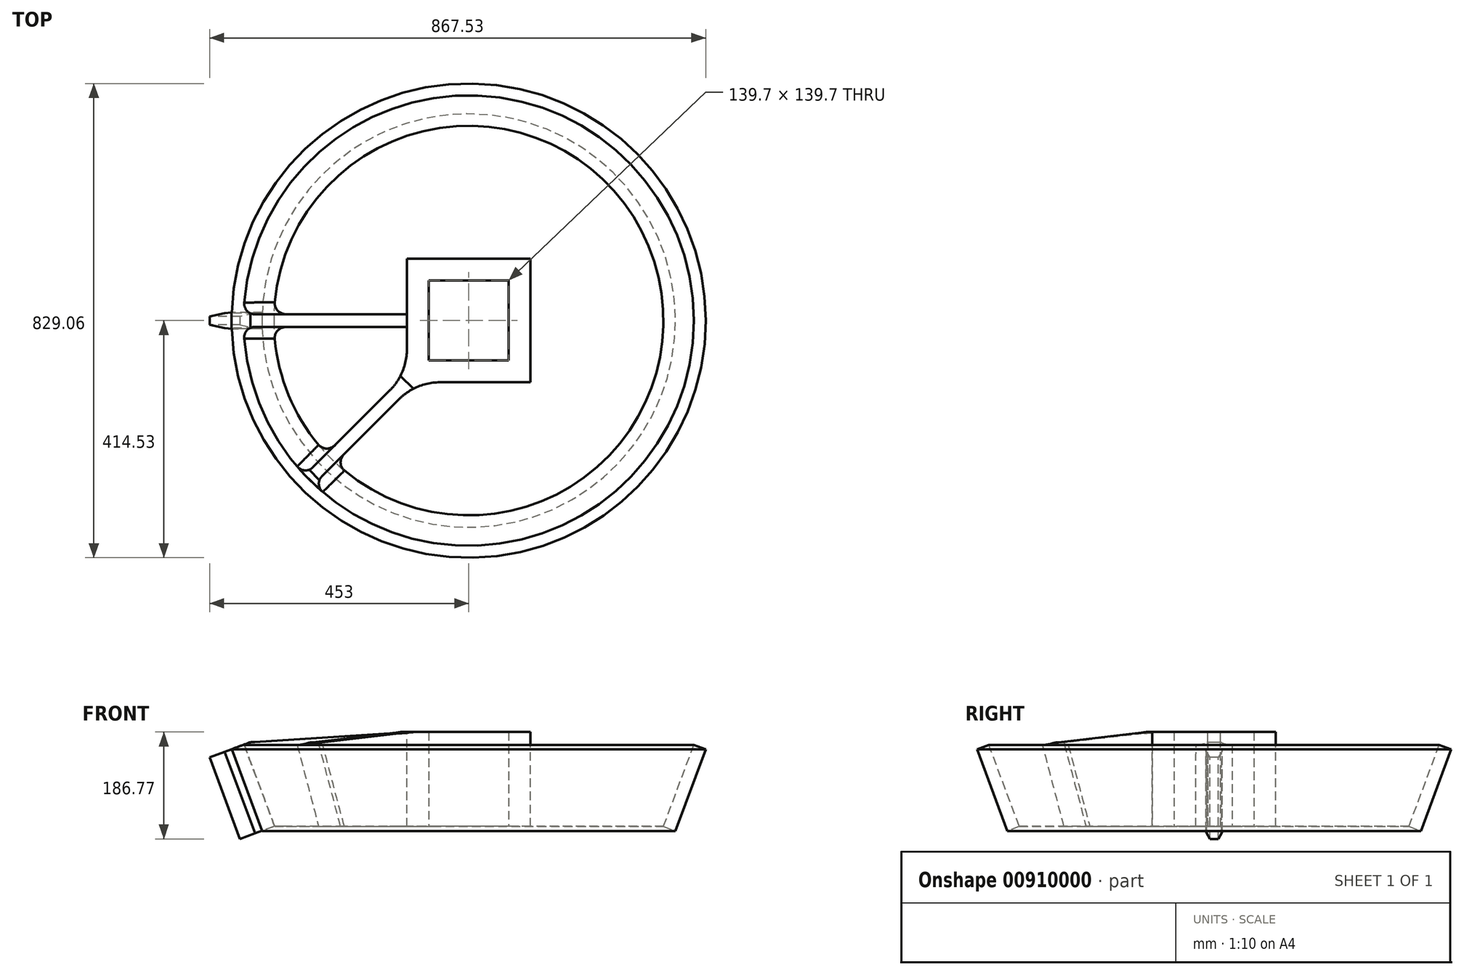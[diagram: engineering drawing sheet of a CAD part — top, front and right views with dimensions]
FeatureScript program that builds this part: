
annotation { "Feature Type Name" : "Feature", "Feature Type Description" : "" }
export const myFeature = defineFeature(function(context is Context, id is Id, definition is map)
    precondition{}
    {
        {
            var Q0;
            Q0=qCreatedBy(makeId("Front.planeOp"),FACE);
            var sketch = newSketch(context, id + "F0", { "sketchPlane" : qUnion([Q0])});
            skLineSegment(sketch, "E0.bottom", {"start": v(107.95, 0) * mm, "end": v(69.85, 0) * mm});
            skLineSegment(sketch, "E0.top", {"start": v(107.95, 165.1) * mm, "end": v(69.85, 165.1) * mm});
            skLineSegment(sketch, "E0.left", {"start": v(107.95, 0) * mm, "end": v(107.95, 165.1) * mm});
            skLineSegment(sketch, "E0.right", {"start": v(-107.95, 0) * mm, "end": v(-107.95, 165.1) * mm});
            skLineSegment(sketch, "E1", {"start": v(-69.85, 165.1) * mm, "end": v(-69.85, 0) * mm});
            skLineSegment(sketch, "E2", {"start": v(69.85, 165.1) * mm, "end": v(69.85, 0) * mm});
            skLineSegment(sketch, "E3", {"start": v(-69.85, 165.1) * mm, "end": v(-107.95, 165.1) * mm});
            skLineSegment(sketch, "E4", {"start": v(69.85, 165.1) * mm, "end": v(-69.85, 165.1) * mm});
            skLineSegment(sketch, "E5", {"start": v(69.85, 0) * mm, "end": v(-69.85, 0) * mm});
            skLineSegment(sketch, "E6", {"start": v(-69.85, 0) * mm, "end": v(-107.95, 0) * mm});
            skLineSegment(sketch, "E7", {"start": v(-340.6, 0) * mm, "end": v(-393.7, 142.85) * mm});
            skLineSegment(sketch, "E8", {"start": v(-393.7, 142.85) * mm, "end": v(-414.53, 135.1) * mm});
            skLineSegment(sketch, "E9", {"start": v(-414.53, 135.1) * mm, "end": v(-361.42, -7.75) * mm});
            skLineSegment(sketch, "E10", {"start": v(-361.42, -7.75) * mm, "end": v(-340.6, 0) * mm});
            skLineSegment(sketch, "E11", {"start": v(0, 0) * mm, "end": v(0, 165.1) * mm, "construction": true});
            skLineSegment(sketch, "E12", {"start": v(-340.6, 0) * mm, "end": v(-107.95, 0) * mm});
            skLineSegment(sketch, "E13", {"start": v(-393.7, 142.85) * mm, "end": v(-381.8, 147.27) * mm});
            skLineSegment(sketch, "E14", {"start": v(-381.8, 147.27) * mm, "end": v(-107.95, 165.1) * mm});
            skLineSegment(sketch, "E15", {"start": v(-381.8, 147.27) * mm, "end": v(-386.22, 159.18) * mm});
            skLineSegment(sketch, "E16", {"start": v(-386.22, 159.18) * mm, "end": v(-418.96, 147) * mm});
            skLineSegment(sketch, "E17", {"start": v(-418.96, 147) * mm, "end": v(-414.53, 135.1) * mm});
            skSolve(sketch);
        }
        {
            var Q0;
            Q0=makeQuery(id+"F0.imprint","IMPRINT",FACE,{"disambiguationData":[TD([[makeQuery(id+"F0.imprint","IMPRINT",EDGE,{"derivedFrom":sQuery(id+"F0.wireOp",EDGE,"E0.right")}),-1.0]])]});
            var Q1;
            Q1=makeQuery(id+"F0.imprint","IMPRINT",FACE,{"disambiguationData":[TD([[makeQuery(id+"F0.imprint","IMPRINT",EDGE,{"derivedFrom":sQuery(id+"F0.wireOp",EDGE,"E1")}),1.0]])]});
            var Q2;
            Q2=makeQuery(id+"F0.imprint","IMPRINT",FACE,{"disambiguationData":[TD([[makeQuery(id+"F0.imprint","IMPRINT",EDGE,{"derivedFrom":sQuery(id+"F0.wireOp",EDGE,"E0.bottom")}),-1.0]])]});
            extrude(context, id + "F1", {"entities" : qUnion([Q0, Q1, Q2]), "depth" : 215.9 * mm, "offsetDistance" : 25 * mm, "symmetric" : true});
        }
        {
            var Q0;
            Q0=makeQuery(id+"F0.imprint","IMPRINT",FACE,{"disambiguationData":[TD([[makeQuery(id+"F0.imprint","IMPRINT",EDGE,{"derivedFrom":sQuery(id+"F0.wireOp",EDGE,"E1")}),1.0]])]});
            extrude(context, id + "F2", {"entities" : qUnion([Q0]), "operationType" : NewBodyOperationType.REMOVE, "oppositeDirection" : true, "depth" : 139.7 * mm, "offsetDistance" : 25 * mm, "symmetric" : true});
        }
        {
            var Q0;
            Q0=makeQuery(id+"F0.imprint","IMPRINT",FACE,{"disambiguationData":[TD([[makeQuery(id+"F0.imprint","IMPRINT",EDGE,{"derivedFrom":sQuery(id+"F0.wireOp",EDGE,"E0.right")}),1.0]])]});
            extrude(context, id + "F3", {"entities" : qUnion([Q0]), "operationType" : NewBodyOperationType.ADD, "depth" : 22.23 * mm, "offsetDistance" : 25 * mm, "symmetric" : true});
        }
        {
            var Q0;
            Q0=makeQuery(id+"F0.imprint","IMPRINT",FACE,{"disambiguationData":[TD([[makeQuery(id+"F0.imprint","IMPRINT",EDGE,{"derivedFrom":sQuery(id+"F0.wireOp",EDGE,"E7")}),1.0]])]});
            var Q1;
            Q1=sQuery(id+"F0.wireOp",EDGE,"E11");
            revolve(context, id + "F4", {"operationType" : NewBodyOperationType.ADD, "surfaceOperationType" : NewSurfaceOperationType.NEW, "entities" : qUnion([Q0]), "axis" : qUnion([Q1]), "revolveType" : RevolveType.FULL});
        }
        {
            var Q0;
            Q0=makeQuery(id+"F1.opExtrude","CAP_VERTEX",VERTEX,{"disambiguationData":[OSD([sQuery(id+"F0.wireOp",EDGE,"E0.right"),sQuery(id+"F0.wireOp",EDGE,"E3"),sQuery(id+"F0.wireOp",EDGE,"E14")])],"isStart":false});
            var Q1;
            Q1=makeQuery(id+"F1.opExtrude","CAP_VERTEX",VERTEX,{"disambiguationData":[OSD([sQuery(id+"F0.wireOp",EDGE,"E0.right"),sQuery(id+"F0.wireOp",EDGE,"E6"),sQuery(id+"F0.wireOp",EDGE,"E12")])],"isStart":false});
            var Q2;
            Q2=makeQuery(id+"F1.opExtrude","CAP_VERTEX",VERTEX,{"disambiguationData":[OSD([sQuery(id+"F0.wireOp",EDGE,"E0.top"),sQuery(id+"F0.wireOp",EDGE,"E0.left")])],"isStart":true});
            cPlane(context, id + "F5", {"entities" : qUnion([Q0, Q1, Q2]), "cplaneType" : CPlaneType.THREE_POINT, "offset" : 25 * mm, "width" : 150 * mm, "height" : 150 * mm});
        }
        {
            var Q0;
            Q0=qCreatedBy(id+"F5.planeOp",FACE);
            var sketch = newSketch(context, id + "F6", { "sketchPlane" : qUnion([Q0])});
            skLineSegment(sketch, "E18", {"start": v(98.78, 165.1) * mm, "end": v(152.66, 165.1) * mm});
            skLineSegment(sketch, "E19", {"start": v(381.8, 146.57) * mm, "end": v(393.7, 142.14) * mm});
            skLineSegment(sketch, "E20", {"start": v(393.7, 142.14) * mm, "end": v(340.85, 0) * mm});
            skLineSegment(sketch, "E21", {"start": v(340.85, 0) * mm, "end": v(98.78, 0) * mm});
            skLineSegment(sketch, "E22", {"start": v(98.78, 0) * mm, "end": v(98.78, 165.1) * mm});
            skLineSegment(sketch, "E23", {"start": v(152.66, 165.1) * mm, "end": v(381.8, 146.57) * mm});
            skSolve(sketch);
        }
        {
            var Q0;
            Q0=makeQuery(id+"F6.imprint","IMPRINT",FACE,{"disambiguationData":[TD([[makeQuery(id+"F6.imprint","IMPRINT",EDGE,{"derivedFrom":sQuery(id+"F6.wireOp",EDGE,"E18")}),-1.0]])]});
            extrude(context, id + "F7", {"entities" : qUnion([Q0]), "operationType" : NewBodyOperationType.ADD, "depth" : 22.23 * mm, "offsetDistance" : 25 * mm, "symmetric" : true});
        }
        {
            var Q0;
            Q0=makeQuery(id+"F3.opExtrude","CAP_EDGE",EDGE,{"disambiguationData":[OSD([sQuery(id+"F0.wireOp",EDGE,"E0.right")])],"isStart":false});
            var Q1;
            Q1=makeQuery(id+"F3.opExtrude","CAP_EDGE",EDGE,{"disambiguationData":[OSD([sQuery(id+"F0.wireOp",EDGE,"E0.right")])],"isStart":true});
            var Q2;
            {var subQ0=sQuery(id+"F0.wireOp",EDGE,"E7");Q2=makeQuery(id+"F4.boolean.opBoolean","INTERSECT",EDGE,{"derivedFrom":[makeQuery(id+"F3.opExtrude","CAP_FACE",FACE,{"disambiguationData":[OSD([sQuery(id+"F0.wireOp",EDGE,"E0.right"),subQ0,sQuery(id+"F0.wireOp",EDGE,"E12"),sQuery(id+"F0.wireOp",EDGE,"E13"),sQuery(id+"F0.wireOp",EDGE,"E14")])],"isStart":true}),makeQuery(id+"F4.opRevolve","SWEPT_FACE",FACE,{"disambiguationData":[OSD([subQ0])]})]});}
            var Q3;
            {var subQ0=sQuery(id+"F0.wireOp",EDGE,"E7");Q3=makeQuery(id+"F4.boolean.opBoolean","INTERSECT",EDGE,{"derivedFrom":[makeQuery(id+"F3.opExtrude","CAP_FACE",FACE,{"disambiguationData":[OSD([sQuery(id+"F0.wireOp",EDGE,"E0.right"),subQ0,sQuery(id+"F0.wireOp",EDGE,"E12"),sQuery(id+"F0.wireOp",EDGE,"E13"),sQuery(id+"F0.wireOp",EDGE,"E14")])],"isStart":false}),makeQuery(id+"F4.opRevolve","SWEPT_FACE",FACE,{"disambiguationData":[OSD([subQ0])]})]});}
            var Q4;
            Q4=makeQuery(id+"F7.boolean.opBoolean","INTERSECT",EDGE,{"derivedFrom":[makeQuery(id+"F4.opRevolve","SWEPT_FACE",FACE,{"disambiguationData":[OSD([sQuery(id+"F0.wireOp",EDGE,"E7")])]}),makeQuery(id+"F7.opExtrude","CAP_FACE",FACE,{"disambiguationData":[OSD([sQuery(id+"F6.wireOp",EDGE,"E18"),sQuery(id+"F6.wireOp",EDGE,"E19"),sQuery(id+"F6.wireOp",EDGE,"E20"),sQuery(id+"F6.wireOp",EDGE,"E21"),sQuery(id+"F6.wireOp",EDGE,"E22"),sQuery(id+"F6.wireOp",EDGE,"E23")])],"isStart":false})]});
            var Q5;
            Q5=makeQuery(id+"F7.boolean.opBoolean","INTERSECT",EDGE,{"derivedFrom":[makeQuery(id+"F4.opRevolve","SWEPT_FACE",FACE,{"disambiguationData":[OSD([sQuery(id+"F0.wireOp",EDGE,"E7")])]}),makeQuery(id+"F7.opExtrude","CAP_FACE",FACE,{"disambiguationData":[OSD([sQuery(id+"F6.wireOp",EDGE,"E18"),sQuery(id+"F6.wireOp",EDGE,"E19"),sQuery(id+"F6.wireOp",EDGE,"E20"),sQuery(id+"F6.wireOp",EDGE,"E21"),sQuery(id+"F6.wireOp",EDGE,"E22"),sQuery(id+"F6.wireOp",EDGE,"E23")])],"isStart":true})]});
            var Q6;
            {var subQ0=sQuery(id+"F6.wireOp",EDGE,"E21");var subQ2=sQuery(id+"F0.wireOp",EDGE,"E12");var subQ9=sQuery(id+"F0.wireOp",EDGE,"E14");var subQ10=sQuery(id+"F0.wireOp",EDGE,"E13");var subQ11=sQuery(id+"F0.wireOp",EDGE,"E7");var subQ12=sQuery(id+"F0.wireOp",EDGE,"E0.right");var subQ13=makeQuery(id+"F3.opExtrude","CAP_FACE",FACE,{"disambiguationData":[OSD([subQ12,subQ11,subQ2,subQ10,subQ9])],"isStart":true});Q6=makeQuery(id+"FeQxwqO8TE0xPhn_1.3.F7.boolean.opBoolean","INTERSECT",EDGE,{"derivedFrom":[makeQuery(id+"FeQxwqO8TE0xPhn_1.3.F3.boolean.opBoolean","SPLIT",FACE,{"disambiguationData":[TD([subQ13])],"derivedFrom":makeQuery(id+"FeQxwqO8TE0xPhn_1.2.F3.boolean.opBoolean","SPLIT",FACE,{"disambiguationData":[TD([subQ13])],"derivedFrom":makeQuery(id+"FeQxwqO8TE0xPhn_1.1.F3.boolean.opBoolean","SPLIT",FACE,{"disambiguationData":[TD([subQ13])],"derivedFrom":makeQuery(id+"F4.opRevolve","SWEPT_FACE",FACE,{"disambiguationData":[OSD([subQ11])]})})})}),makeQuery(id+"FeQxwqO8TE0xPhn_1.3.F7.opExtrude","CAP_FACE",FACE,{"disambiguationData":[OSD([sQuery(id+"F6.wireOp",EDGE,"E18"),sQuery(id+"F6.wireOp",EDGE,"E19"),sQuery(id+"F6.wireOp",EDGE,"E20"),subQ0,sQuery(id+"F6.wireOp",EDGE,"E22"),sQuery(id+"F6.wireOp",EDGE,"E23")])],"isStart":true})]});}
            var Q7;
            {var subQ0=sQuery(id+"F6.wireOp",EDGE,"E21");var subQ2=sQuery(id+"F0.wireOp",EDGE,"E12");var subQ9=sQuery(id+"F0.wireOp",EDGE,"E14");var subQ10=sQuery(id+"F0.wireOp",EDGE,"E13");var subQ11=sQuery(id+"F0.wireOp",EDGE,"E7");var subQ12=sQuery(id+"F0.wireOp",EDGE,"E0.right");var subQ13=makeQuery(id+"F3.opExtrude","CAP_FACE",FACE,{"disambiguationData":[OSD([subQ12,subQ11,subQ2,subQ10,subQ9])],"isStart":true});Q7=makeQuery(id+"FeQxwqO8TE0xPhn_1.3.F7.boolean.opBoolean","INTERSECT",EDGE,{"derivedFrom":[makeQuery(id+"FeQxwqO8TE0xPhn_1.3.F3.boolean.opBoolean","SPLIT",FACE,{"disambiguationData":[TD([subQ13])],"derivedFrom":makeQuery(id+"FeQxwqO8TE0xPhn_1.2.F3.boolean.opBoolean","SPLIT",FACE,{"disambiguationData":[TD([subQ13])],"derivedFrom":makeQuery(id+"FeQxwqO8TE0xPhn_1.1.F3.boolean.opBoolean","SPLIT",FACE,{"disambiguationData":[TD([subQ13])],"derivedFrom":makeQuery(id+"F4.opRevolve","SWEPT_FACE",FACE,{"disambiguationData":[OSD([subQ11])]})})})}),makeQuery(id+"FeQxwqO8TE0xPhn_1.3.F7.opExtrude","CAP_FACE",FACE,{"disambiguationData":[OSD([sQuery(id+"F6.wireOp",EDGE,"E18"),sQuery(id+"F6.wireOp",EDGE,"E19"),sQuery(id+"F6.wireOp",EDGE,"E20"),subQ0,sQuery(id+"F6.wireOp",EDGE,"E22"),sQuery(id+"F6.wireOp",EDGE,"E23")])],"isStart":false})]});}
            var Q8;
            {var subQ0=sQuery(id+"F0.wireOp",EDGE,"E14");var subQ1=sQuery(id+"F0.wireOp",EDGE,"E13");var subQ2=sQuery(id+"F0.wireOp",EDGE,"E12");var subQ3=sQuery(id+"F0.wireOp",EDGE,"E7");var subQ4=sQuery(id+"F0.wireOp",EDGE,"E0.right");var subQ6=makeQuery(id+"F3.opExtrude","CAP_FACE",FACE,{"disambiguationData":[OSD([subQ4,subQ3,subQ2,subQ1,subQ0])],"isStart":true});Q8=makeQuery(id+"FeQxwqO8TE0xPhn_1.3.F3.boolean.opBoolean","INTERSECT",EDGE,{"derivedFrom":[makeQuery(id+"FeQxwqO8TE0xPhn_1.2.F3.boolean.opBoolean","SPLIT",FACE,{"disambiguationData":[TD([subQ6])],"derivedFrom":makeQuery(id+"FeQxwqO8TE0xPhn_1.1.F3.boolean.opBoolean","SPLIT",FACE,{"disambiguationData":[TD([subQ6])],"derivedFrom":makeQuery(id+"F4.opRevolve","SWEPT_FACE",FACE,{"disambiguationData":[OSD([subQ3])]})})}),makeQuery(id+"FeQxwqO8TE0xPhn_1.3.F3.opExtrude","CAP_FACE",FACE,{"disambiguationData":[OSD([subQ4,subQ3,subQ2,subQ1,subQ0])],"isStart":false})]});}
            var Q9;
            {var subQ0=sQuery(id+"F0.wireOp",EDGE,"E14");var subQ1=sQuery(id+"F0.wireOp",EDGE,"E13");var subQ2=sQuery(id+"F0.wireOp",EDGE,"E12");var subQ3=sQuery(id+"F0.wireOp",EDGE,"E7");var subQ4=sQuery(id+"F0.wireOp",EDGE,"E0.right");var subQ6=makeQuery(id+"F3.opExtrude","CAP_FACE",FACE,{"disambiguationData":[OSD([subQ4,subQ3,subQ2,subQ1,subQ0])],"isStart":true});Q9=makeQuery(id+"FeQxwqO8TE0xPhn_1.3.F3.boolean.opBoolean","INTERSECT",EDGE,{"derivedFrom":[makeQuery(id+"FeQxwqO8TE0xPhn_1.2.F3.boolean.opBoolean","SPLIT",FACE,{"disambiguationData":[TD([subQ6])],"derivedFrom":makeQuery(id+"FeQxwqO8TE0xPhn_1.1.F3.boolean.opBoolean","SPLIT",FACE,{"disambiguationData":[TD([subQ6])],"derivedFrom":makeQuery(id+"F4.opRevolve","SWEPT_FACE",FACE,{"disambiguationData":[OSD([subQ3])]})})}),makeQuery(id+"FeQxwqO8TE0xPhn_1.3.F3.opExtrude","CAP_FACE",FACE,{"disambiguationData":[OSD([subQ4,subQ3,subQ2,subQ1,subQ0])],"isStart":true})]});}
            var Q10;
            Q10=makeQuery(id+"FeQxwqO8TE0xPhn_1.3.F3.opExtrude","CAP_EDGE",EDGE,{"disambiguationData":[OSD([sQuery(id+"F0.wireOp",EDGE,"E0.right")])],"isStart":true});
            var Q11;
            Q11=makeQuery(id+"FeQxwqO8TE0xPhn_1.3.F3.opExtrude","CAP_EDGE",EDGE,{"disambiguationData":[OSD([sQuery(id+"F0.wireOp",EDGE,"E0.right")])],"isStart":false});
            var Q12;
            {var subQ0=sQuery(id+"F6.wireOp",EDGE,"E21");var subQ2=sQuery(id+"F0.wireOp",EDGE,"E14");var subQ3=sQuery(id+"F0.wireOp",EDGE,"E13");var subQ4=sQuery(id+"F0.wireOp",EDGE,"E12");var subQ5=sQuery(id+"F0.wireOp",EDGE,"E7");var subQ6=sQuery(id+"F0.wireOp",EDGE,"E0.right");var subQ7=makeQuery(id+"F3.opExtrude","CAP_FACE",FACE,{"disambiguationData":[OSD([subQ6,subQ5,subQ4,subQ3,subQ2])],"isStart":true});Q12=makeQuery(id+"FeQxwqO8TE0xPhn_1.2.F7.boolean.opBoolean","INTERSECT",EDGE,{"derivedFrom":[makeQuery(id+"FeQxwqO8TE0xPhn_1.2.F3.boolean.opBoolean","SPLIT",FACE,{"disambiguationData":[TD([subQ7])],"derivedFrom":makeQuery(id+"FeQxwqO8TE0xPhn_1.1.F3.boolean.opBoolean","SPLIT",FACE,{"disambiguationData":[TD([subQ7])],"derivedFrom":makeQuery(id+"F4.opRevolve","SWEPT_FACE",FACE,{"disambiguationData":[OSD([subQ5])]})})}),makeQuery(id+"FeQxwqO8TE0xPhn_1.2.F7.opExtrude","CAP_FACE",FACE,{"disambiguationData":[OSD([sQuery(id+"F6.wireOp",EDGE,"E18"),sQuery(id+"F6.wireOp",EDGE,"E19"),sQuery(id+"F6.wireOp",EDGE,"E20"),subQ0,sQuery(id+"F6.wireOp",EDGE,"E22"),sQuery(id+"F6.wireOp",EDGE,"E23")])],"isStart":true})]});}
            var Q13;
            {var subQ0=sQuery(id+"F6.wireOp",EDGE,"E21");var subQ2=sQuery(id+"F0.wireOp",EDGE,"E14");var subQ3=sQuery(id+"F0.wireOp",EDGE,"E13");var subQ4=sQuery(id+"F0.wireOp",EDGE,"E12");var subQ5=sQuery(id+"F0.wireOp",EDGE,"E7");var subQ6=sQuery(id+"F0.wireOp",EDGE,"E0.right");var subQ7=makeQuery(id+"F3.opExtrude","CAP_FACE",FACE,{"disambiguationData":[OSD([subQ6,subQ5,subQ4,subQ3,subQ2])],"isStart":true});Q13=makeQuery(id+"FeQxwqO8TE0xPhn_1.2.F7.boolean.opBoolean","INTERSECT",EDGE,{"derivedFrom":[makeQuery(id+"FeQxwqO8TE0xPhn_1.2.F3.boolean.opBoolean","SPLIT",FACE,{"disambiguationData":[TD([subQ7])],"derivedFrom":makeQuery(id+"FeQxwqO8TE0xPhn_1.1.F3.boolean.opBoolean","SPLIT",FACE,{"disambiguationData":[TD([subQ7])],"derivedFrom":makeQuery(id+"F4.opRevolve","SWEPT_FACE",FACE,{"disambiguationData":[OSD([subQ5])]})})}),makeQuery(id+"FeQxwqO8TE0xPhn_1.2.F7.opExtrude","CAP_FACE",FACE,{"disambiguationData":[OSD([sQuery(id+"F6.wireOp",EDGE,"E18"),sQuery(id+"F6.wireOp",EDGE,"E19"),sQuery(id+"F6.wireOp",EDGE,"E20"),subQ0,sQuery(id+"F6.wireOp",EDGE,"E22"),sQuery(id+"F6.wireOp",EDGE,"E23")])],"isStart":false})]});}
            var Q14;
            Q14=makeQuery(id+"FeQxwqO8TE0xPhn_1.2.F3.opExtrude","CAP_EDGE",EDGE,{"disambiguationData":[OSD([sQuery(id+"F0.wireOp",EDGE,"E0.right")])],"isStart":false});
            var Q15;
            {var subQ0=sQuery(id+"F0.wireOp",EDGE,"E14");var subQ1=sQuery(id+"F0.wireOp",EDGE,"E13");var subQ2=sQuery(id+"F0.wireOp",EDGE,"E12");var subQ3=sQuery(id+"F0.wireOp",EDGE,"E7");var subQ4=sQuery(id+"F0.wireOp",EDGE,"E0.right");Q15=makeQuery(id+"FeQxwqO8TE0xPhn_1.2.F3.boolean.opBoolean","INTERSECT",EDGE,{"derivedFrom":[makeQuery(id+"FeQxwqO8TE0xPhn_1.1.F3.boolean.opBoolean","SPLIT",FACE,{"disambiguationData":[TD([makeQuery(id+"F3.opExtrude","CAP_FACE",FACE,{"disambiguationData":[OSD([subQ4,subQ3,subQ2,subQ1,subQ0])],"isStart":true})])],"derivedFrom":makeQuery(id+"F4.opRevolve","SWEPT_FACE",FACE,{"disambiguationData":[OSD([subQ3])]})}),makeQuery(id+"FeQxwqO8TE0xPhn_1.2.F3.opExtrude","CAP_FACE",FACE,{"disambiguationData":[OSD([subQ4,subQ3,subQ2,subQ1,subQ0])],"isStart":false})]});}
            var Q16;
            Q16=makeQuery(id+"FeQxwqO8TE0xPhn_1.2.F3.opExtrude","CAP_EDGE",EDGE,{"disambiguationData":[OSD([sQuery(id+"F0.wireOp",EDGE,"E0.right")])],"isStart":true});
            var Q17;
            Q17=makeQuery(id+"FeQxwqO8TE0xPhn_1.1.F3.opExtrude","CAP_EDGE",EDGE,{"disambiguationData":[OSD([sQuery(id+"F0.wireOp",EDGE,"E0.right")])],"isStart":false});
            var Q18;
            Q18=makeQuery(id+"FeQxwqO8TE0xPhn_1.1.F3.opExtrude","CAP_EDGE",EDGE,{"disambiguationData":[OSD([sQuery(id+"F0.wireOp",EDGE,"E0.right")])],"isStart":true});
            var Q19;
            {var subQ0=sQuery(id+"F0.wireOp",EDGE,"E7");Q19=makeQuery(id+"FeQxwqO8TE0xPhn_1.1.F3.boolean.opBoolean","INTERSECT",EDGE,{"derivedFrom":[makeQuery(id+"F4.opRevolve","SWEPT_FACE",FACE,{"disambiguationData":[OSD([subQ0])]}),makeQuery(id+"FeQxwqO8TE0xPhn_1.1.F3.opExtrude","CAP_FACE",FACE,{"disambiguationData":[OSD([sQuery(id+"F0.wireOp",EDGE,"E0.right"),subQ0,sQuery(id+"F0.wireOp",EDGE,"E12"),sQuery(id+"F0.wireOp",EDGE,"E13"),sQuery(id+"F0.wireOp",EDGE,"E14")])],"isStart":true})]});}
            var Q20;
            {var subQ0=sQuery(id+"F6.wireOp",EDGE,"E21");var subQ1=sQuery(id+"F0.wireOp",EDGE,"E14");var subQ2=sQuery(id+"F0.wireOp",EDGE,"E13");var subQ3=sQuery(id+"F0.wireOp",EDGE,"E12");var subQ4=sQuery(id+"F0.wireOp",EDGE,"E7");var subQ5=sQuery(id+"F0.wireOp",EDGE,"E0.right");Q20=makeQuery(id+"FeQxwqO8TE0xPhn_1.1.F7.boolean.opBoolean","INTERSECT",EDGE,{"derivedFrom":[makeQuery(id+"FeQxwqO8TE0xPhn_1.1.F3.boolean.opBoolean","SPLIT",FACE,{"disambiguationData":[TD([makeQuery(id+"F3.opExtrude","CAP_FACE",FACE,{"disambiguationData":[OSD([subQ5,subQ4,subQ3,subQ2,subQ1])],"isStart":true})])],"derivedFrom":makeQuery(id+"F4.opRevolve","SWEPT_FACE",FACE,{"disambiguationData":[OSD([subQ4])]})}),makeQuery(id+"FeQxwqO8TE0xPhn_1.1.F7.opExtrude","CAP_FACE",FACE,{"disambiguationData":[OSD([sQuery(id+"F6.wireOp",EDGE,"E18"),sQuery(id+"F6.wireOp",EDGE,"E19"),sQuery(id+"F6.wireOp",EDGE,"E20"),subQ0,sQuery(id+"F6.wireOp",EDGE,"E22"),sQuery(id+"F6.wireOp",EDGE,"E23")])],"isStart":false})]});}
            var Q21;
            {var subQ0=sQuery(id+"F0.wireOp",EDGE,"E14");var subQ1=sQuery(id+"F0.wireOp",EDGE,"E13");var subQ2=sQuery(id+"F0.wireOp",EDGE,"E12");var subQ3=sQuery(id+"F0.wireOp",EDGE,"E7");var subQ4=sQuery(id+"F0.wireOp",EDGE,"E0.right");Q21=makeQuery(id+"FeQxwqO8TE0xPhn_1.2.F3.boolean.opBoolean","INTERSECT",EDGE,{"derivedFrom":[makeQuery(id+"FeQxwqO8TE0xPhn_1.1.F3.boolean.opBoolean","SPLIT",FACE,{"disambiguationData":[TD([makeQuery(id+"F3.opExtrude","CAP_FACE",FACE,{"disambiguationData":[OSD([subQ4,subQ3,subQ2,subQ1,subQ0])],"isStart":true})])],"derivedFrom":makeQuery(id+"F4.opRevolve","SWEPT_FACE",FACE,{"disambiguationData":[OSD([subQ3])]})}),makeQuery(id+"FeQxwqO8TE0xPhn_1.2.F3.opExtrude","CAP_FACE",FACE,{"disambiguationData":[OSD([subQ4,subQ3,subQ2,subQ1,subQ0])],"isStart":true})]});}
            var Q22;
            {var subQ0=sQuery(id+"F6.wireOp",EDGE,"E21");var subQ1=sQuery(id+"F0.wireOp",EDGE,"E14");var subQ2=sQuery(id+"F0.wireOp",EDGE,"E13");var subQ3=sQuery(id+"F0.wireOp",EDGE,"E12");var subQ4=sQuery(id+"F0.wireOp",EDGE,"E7");var subQ5=sQuery(id+"F0.wireOp",EDGE,"E0.right");Q22=makeQuery(id+"FeQxwqO8TE0xPhn_1.1.F7.boolean.opBoolean","INTERSECT",EDGE,{"derivedFrom":[makeQuery(id+"FeQxwqO8TE0xPhn_1.1.F3.boolean.opBoolean","SPLIT",FACE,{"disambiguationData":[TD([makeQuery(id+"F3.opExtrude","CAP_FACE",FACE,{"disambiguationData":[OSD([subQ5,subQ4,subQ3,subQ2,subQ1])],"isStart":true})])],"derivedFrom":makeQuery(id+"F4.opRevolve","SWEPT_FACE",FACE,{"disambiguationData":[OSD([subQ4])]})}),makeQuery(id+"FeQxwqO8TE0xPhn_1.1.F7.opExtrude","CAP_FACE",FACE,{"disambiguationData":[OSD([sQuery(id+"F6.wireOp",EDGE,"E18"),sQuery(id+"F6.wireOp",EDGE,"E19"),sQuery(id+"F6.wireOp",EDGE,"E20"),subQ0,sQuery(id+"F6.wireOp",EDGE,"E22"),sQuery(id+"F6.wireOp",EDGE,"E23")])],"isStart":true})]});}
            var Q23;
            {var subQ0=sQuery(id+"F0.wireOp",EDGE,"E7");Q23=makeQuery(id+"FeQxwqO8TE0xPhn_1.1.F3.boolean.opBoolean","INTERSECT",EDGE,{"derivedFrom":[makeQuery(id+"F4.opRevolve","SWEPT_FACE",FACE,{"disambiguationData":[OSD([subQ0])]}),makeQuery(id+"FeQxwqO8TE0xPhn_1.1.F3.opExtrude","CAP_FACE",FACE,{"disambiguationData":[OSD([sQuery(id+"F0.wireOp",EDGE,"E0.right"),subQ0,sQuery(id+"F0.wireOp",EDGE,"E12"),sQuery(id+"F0.wireOp",EDGE,"E13"),sQuery(id+"F0.wireOp",EDGE,"E14")])],"isStart":false})]});}
            fillet(context, id + "F8", {"entities" : qUnion([Q0, Q1, Q2, Q3, Q4, Q5, Q6, Q7, Q8, Q9, Q10, Q11, Q12, Q13, Q14, Q15, Q16, Q17, Q18, Q19, Q20, Q21, Q22, Q23]), "radius" : 19.05 * mm, "tangentPropagation" : true, "allowEdgeOverflow" : false});
        }
        {
            var Q0;
            Q0=makeQuery(id+"F7.boolean.opBoolean","INTERSECT",EDGE,{"derivedFrom":[makeQuery(id+"F1.opExtrude","CAP_FACE",FACE,{"disambiguationData":[OSD([sQuery(id+"F0.wireOp",EDGE,"E0.bottom"),sQuery(id+"F0.wireOp",EDGE,"E0.top"),sQuery(id+"F0.wireOp",EDGE,"E0.left"),sQuery(id+"F0.wireOp",EDGE,"E0.right"),sQuery(id+"F0.wireOp",EDGE,"E3"),sQuery(id+"F0.wireOp",EDGE,"E4"),sQuery(id+"F0.wireOp",EDGE,"E5"),sQuery(id+"F0.wireOp",EDGE,"E6")])],"isStart":false}),makeQuery(id+"F7.opExtrude","CAP_FACE",FACE,{"disambiguationData":[OSD([sQuery(id+"F6.wireOp",EDGE,"E18"),sQuery(id+"F6.wireOp",EDGE,"E19"),sQuery(id+"F6.wireOp",EDGE,"E20"),sQuery(id+"F6.wireOp",EDGE,"E21"),sQuery(id+"F6.wireOp",EDGE,"E22"),sQuery(id+"F6.wireOp",EDGE,"E23")])],"isStart":true})]});
            var Q1;
            {var subQ0=sQuery(id+"F0.wireOp",EDGE,"E14");var subQ1=sQuery(id+"F0.wireOp",EDGE,"E12");var subQ2=sQuery(id+"F0.wireOp",EDGE,"E0.right");Q1=makeQuery(id+"F7.boolean.opBoolean","INTERSECT",EDGE,{"derivedFrom":[makeQuery(id+"F3.boolean.opBoolean","SPLIT",FACE,{"disambiguationData":[TD([makeQuery(id+"F3.opExtrude","CAP_FACE",FACE,{"disambiguationData":[OSD([subQ2,sQuery(id+"F0.wireOp",EDGE,"E7"),subQ1,sQuery(id+"F0.wireOp",EDGE,"E13"),subQ0])],"isStart":false})])],"derivedFrom":makeQuery(id+"F1.opExtrude","SWEPT_FACE",FACE,{"disambiguationData":[OSD([subQ2])]})}),makeQuery(id+"F7.opExtrude","CAP_FACE",FACE,{"disambiguationData":[OSD([sQuery(id+"F6.wireOp",EDGE,"E18"),sQuery(id+"F6.wireOp",EDGE,"E19"),sQuery(id+"F6.wireOp",EDGE,"E20"),sQuery(id+"F6.wireOp",EDGE,"E21"),sQuery(id+"F6.wireOp",EDGE,"E22"),sQuery(id+"F6.wireOp",EDGE,"E23")])],"isStart":false})]});}
            var Q2;
            {var subQ0=sQuery(id+"F0.wireOp",EDGE,"E14");var subQ1=sQuery(id+"F0.wireOp",EDGE,"E12");var subQ2=sQuery(id+"F0.wireOp",EDGE,"E0.right");Q2=makeQuery(id+"FeQxwqO8TE0xPhn_1.3.F7.boolean.opBoolean","INTERSECT",EDGE,{"derivedFrom":[makeQuery(id+"F3.boolean.opBoolean","SPLIT",FACE,{"disambiguationData":[TD([makeQuery(id+"F3.opExtrude","CAP_FACE",FACE,{"disambiguationData":[OSD([subQ2,sQuery(id+"F0.wireOp",EDGE,"E7"),subQ1,sQuery(id+"F0.wireOp",EDGE,"E13"),subQ0])],"isStart":true})])],"derivedFrom":makeQuery(id+"F1.opExtrude","SWEPT_FACE",FACE,{"disambiguationData":[OSD([subQ2])]})}),makeQuery(id+"FeQxwqO8TE0xPhn_1.3.F7.opExtrude","CAP_FACE",FACE,{"disambiguationData":[OSD([sQuery(id+"F6.wireOp",EDGE,"E18"),sQuery(id+"F6.wireOp",EDGE,"E19"),sQuery(id+"F6.wireOp",EDGE,"E20"),sQuery(id+"F6.wireOp",EDGE,"E21"),sQuery(id+"F6.wireOp",EDGE,"E22"),sQuery(id+"F6.wireOp",EDGE,"E23")])],"isStart":true})]});}
            var Q3;
            {var subQ0=sQuery(id+"F6.wireOp",EDGE,"E21");var subQ1=sQuery(id+"F6.wireOp",EDGE,"E18");var subQ3=sQuery(id+"F0.wireOp",EDGE,"E4");var subQ4=sQuery(id+"F0.wireOp",EDGE,"E3");var subQ5=sQuery(id+"F0.wireOp",EDGE,"E0.top");var subQ7=sQuery(id+"F0.wireOp",EDGE,"E0.right");var subQ8=sQuery(id+"F0.wireOp",EDGE,"E6");var subQ9=sQuery(id+"F0.wireOp",EDGE,"E5");var subQ10=sQuery(id+"F0.wireOp",EDGE,"E0.bottom");Q3=makeQuery(id+"FeQxwqO8TE0xPhn_1.3.F7.boolean.opBoolean","INTERSECT",EDGE,{"derivedFrom":[makeQuery(id+"FeQxwqO8TE0xPhn_1.3.F3.boolean.opBoolean","SPLIT",FACE,{"disambiguationData":[TD([makeQuery(id+"F1.opExtrude","SWEPT_FACE",FACE,{"disambiguationData":[OSD([subQ7])]})])],"derivedFrom":makeQuery(id+"F1.opExtrude","CAP_FACE",FACE,{"disambiguationData":[OSD([subQ10,subQ5,sQuery(id+"F0.wireOp",EDGE,"E0.left"),subQ7,subQ4,subQ3,subQ9,subQ8])],"isStart":true})}),makeQuery(id+"FeQxwqO8TE0xPhn_1.3.F7.opExtrude","CAP_FACE",FACE,{"disambiguationData":[OSD([subQ1,sQuery(id+"F6.wireOp",EDGE,"E19"),sQuery(id+"F6.wireOp",EDGE,"E20"),subQ0,sQuery(id+"F6.wireOp",EDGE,"E22"),sQuery(id+"F6.wireOp",EDGE,"E23")])],"isStart":false})]});}
            var Q4;
            Q4=makeQuery(id+"FeQxwqO8TE0xPhn_1.2.F7.boolean.opBoolean","INTERSECT",EDGE,{"derivedFrom":[makeQuery(id+"F1.opExtrude","CAP_FACE",FACE,{"disambiguationData":[OSD([sQuery(id+"F0.wireOp",EDGE,"E0.bottom"),sQuery(id+"F0.wireOp",EDGE,"E0.top"),sQuery(id+"F0.wireOp",EDGE,"E0.left"),sQuery(id+"F0.wireOp",EDGE,"E0.right"),sQuery(id+"F0.wireOp",EDGE,"E3"),sQuery(id+"F0.wireOp",EDGE,"E4"),sQuery(id+"F0.wireOp",EDGE,"E5"),sQuery(id+"F0.wireOp",EDGE,"E6")])],"isStart":true}),makeQuery(id+"FeQxwqO8TE0xPhn_1.2.F7.opExtrude","CAP_FACE",FACE,{"disambiguationData":[OSD([sQuery(id+"F6.wireOp",EDGE,"E18"),sQuery(id+"F6.wireOp",EDGE,"E19"),sQuery(id+"F6.wireOp",EDGE,"E20"),sQuery(id+"F6.wireOp",EDGE,"E21"),sQuery(id+"F6.wireOp",EDGE,"E22"),sQuery(id+"F6.wireOp",EDGE,"E23")])],"isStart":true})]});
            var Q5;
            {var subQ0=sQuery(id+"F6.wireOp",EDGE,"E21");var subQ1=sQuery(id+"F6.wireOp",EDGE,"E18");var subQ2=sQuery(id+"F0.wireOp",EDGE,"E12");var subQ6=sQuery(id+"F0.wireOp",EDGE,"E14");var subQ7=sQuery(id+"F0.wireOp",EDGE,"E0.right");var subQ10=sQuery(id+"F0.wireOp",EDGE,"E0.left");Q5=makeQuery(id+"FeQxwqO8TE0xPhn_1.2.F7.boolean.opBoolean","INTERSECT",EDGE,{"derivedFrom":[makeQuery(id+"FeQxwqO8TE0xPhn_1.2.F3.boolean.opBoolean","SPLIT",FACE,{"disambiguationData":[TD([makeQuery(id+"FeQxwqO8TE0xPhn_1.2.F3.opExtrude","CAP_FACE",FACE,{"disambiguationData":[OSD([subQ7,sQuery(id+"F0.wireOp",EDGE,"E7"),subQ2,sQuery(id+"F0.wireOp",EDGE,"E13"),subQ6])],"isStart":false})])],"derivedFrom":makeQuery(id+"F1.opExtrude","SWEPT_FACE",FACE,{"disambiguationData":[OSD([subQ10])]})}),makeQuery(id+"FeQxwqO8TE0xPhn_1.2.F7.opExtrude","CAP_FACE",FACE,{"disambiguationData":[OSD([subQ1,sQuery(id+"F6.wireOp",EDGE,"E19"),sQuery(id+"F6.wireOp",EDGE,"E20"),subQ0,sQuery(id+"F6.wireOp",EDGE,"E22"),sQuery(id+"F6.wireOp",EDGE,"E23")])],"isStart":false})]});}
            var Q6;
            Q6=makeQuery(id+"FeQxwqO8TE0xPhn_1.1.F7.boolean.opBoolean","INTERSECT",EDGE,{"derivedFrom":[makeQuery(id+"F1.opExtrude","SWEPT_FACE",FACE,{"disambiguationData":[OSD([sQuery(id+"F0.wireOp",EDGE,"E0.left")])]}),makeQuery(id+"FeQxwqO8TE0xPhn_1.1.F7.opExtrude","CAP_FACE",FACE,{"disambiguationData":[OSD([sQuery(id+"F6.wireOp",EDGE,"E18"),sQuery(id+"F6.wireOp",EDGE,"E19"),sQuery(id+"F6.wireOp",EDGE,"E20"),sQuery(id+"F6.wireOp",EDGE,"E21"),sQuery(id+"F6.wireOp",EDGE,"E22"),sQuery(id+"F6.wireOp",EDGE,"E23")])],"isStart":true})]});
            var Q7;
            {var subQ0=sQuery(id+"F6.wireOp",EDGE,"E21");var subQ1=sQuery(id+"F6.wireOp",EDGE,"E18");var subQ2=sQuery(id+"F0.wireOp",EDGE,"E0.left");var subQ3=sQuery(id+"F0.wireOp",EDGE,"E4");var subQ4=sQuery(id+"F0.wireOp",EDGE,"E3");var subQ5=sQuery(id+"F0.wireOp",EDGE,"E0.top");var subQ7=sQuery(id+"F0.wireOp",EDGE,"E6");var subQ8=sQuery(id+"F0.wireOp",EDGE,"E5");var subQ9=sQuery(id+"F0.wireOp",EDGE,"E0.bottom");var subQ11=sQuery(id+"F0.wireOp",EDGE,"E0.right");Q7=makeQuery(id+"FeQxwqO8TE0xPhn_1.1.F7.boolean.opBoolean","INTERSECT",EDGE,{"derivedFrom":[makeQuery(id+"FeQxwqO8TE0xPhn_1.1.F3.boolean.opBoolean","SPLIT",FACE,{"disambiguationData":[TD([makeQuery(id+"F1.opExtrude","SWEPT_FACE",FACE,{"disambiguationData":[OSD([subQ2])]})])],"derivedFrom":makeQuery(id+"F1.opExtrude","CAP_FACE",FACE,{"disambiguationData":[OSD([subQ9,subQ5,subQ2,subQ11,subQ4,subQ3,subQ8,subQ7])],"isStart":false})}),makeQuery(id+"FeQxwqO8TE0xPhn_1.1.F7.opExtrude","CAP_FACE",FACE,{"disambiguationData":[OSD([subQ1,sQuery(id+"F6.wireOp",EDGE,"E19"),sQuery(id+"F6.wireOp",EDGE,"E20"),subQ0,sQuery(id+"F6.wireOp",EDGE,"E22"),sQuery(id+"F6.wireOp",EDGE,"E23")])],"isStart":false})]});}
            fillet(context, id + "F9", {"entities" : qUnion([Q0, Q1, Q2, Q3, Q4, Q5, Q6, Q7]), "radius" : 101.6 * mm, "tangentPropagation" : true, "allowEdgeOverflow" : false});
        }
        {
            var Q0;
            Q0=makeQuery(id+"F3.opExtrude","SWEPT_FACE",FACE,{"disambiguationData":[OSD([sQuery(id+"F0.wireOp",EDGE,"E13")])]});
            var sketch = newSketch(context, id + "F10", { "sketchPlane" : qUnion([Q0])});
            skLineSegment(sketch, "E24", {"start": v(-354.26, 13.15) * mm, "end": v(-382.5, 7.14) * mm});
            skLineSegment(sketch, "E25", {"start": v(-382.5, 7.14) * mm, "end": v(-382.5, -7.14) * mm});
            skLineSegment(sketch, "E26", {"start": v(-382.5, -7.14) * mm, "end": v(-354.26, -13.15) * mm});
            skLineSegment(sketch, "E27", {"start": v(-354.26, -13.15) * mm, "end": v(-341.23, -14.29) * mm});
            skLineSegment(sketch, "E28", {"start": v(-341.23, -14.29) * mm, "end": v(-341.23, 14.29) * mm});
            skLineSegment(sketch, "E29", {"start": v(-341.23, 14.29) * mm, "end": v(-354.26, 13.15) * mm});
            skSolve(sketch);
        }
        {
            var Q0;
            Q0=makeQuery(id+"F10.imprint","IMPRINT",FACE,{"disambiguationData":[TD([[makeQuery(id+"F10.imprint","IMPRINT",EDGE,{"derivedFrom":sQuery(id+"F10.wireOp",EDGE,"E24")}),1.0]])]});
            extrude(context, id + "F11", {"entities" : qUnion([Q0]), "operationType" : NewBodyOperationType.ADD, "oppositeDirection" : true, "depth" : 152 * mm, "offsetDistance" : 25 * mm});
        }
        {
            var Q0;
            Q0=makeQuery(id+"F0.imprint","IMPRINT",FACE,{"disambiguationData":[TD([[makeQuery(id+"F0.imprint","IMPRINT",EDGE,{"derivedFrom":sQuery(id+"F0.wireOp",EDGE,"E8")}),-1.0]])]});
            var Q1;
            Q1=sQuery(id+"F0.wireOp",EDGE,"E11");
            revolve(context, id + "F12", {"operationType" : NewBodyOperationType.REMOVE, "surfaceOperationType" : NewSurfaceOperationType.NEW, "entities" : qUnion([Q0]), "axis" : qUnion([Q1]), "revolveType" : RevolveType.FULL, "oppositeDirection" : true});
        }
    });
